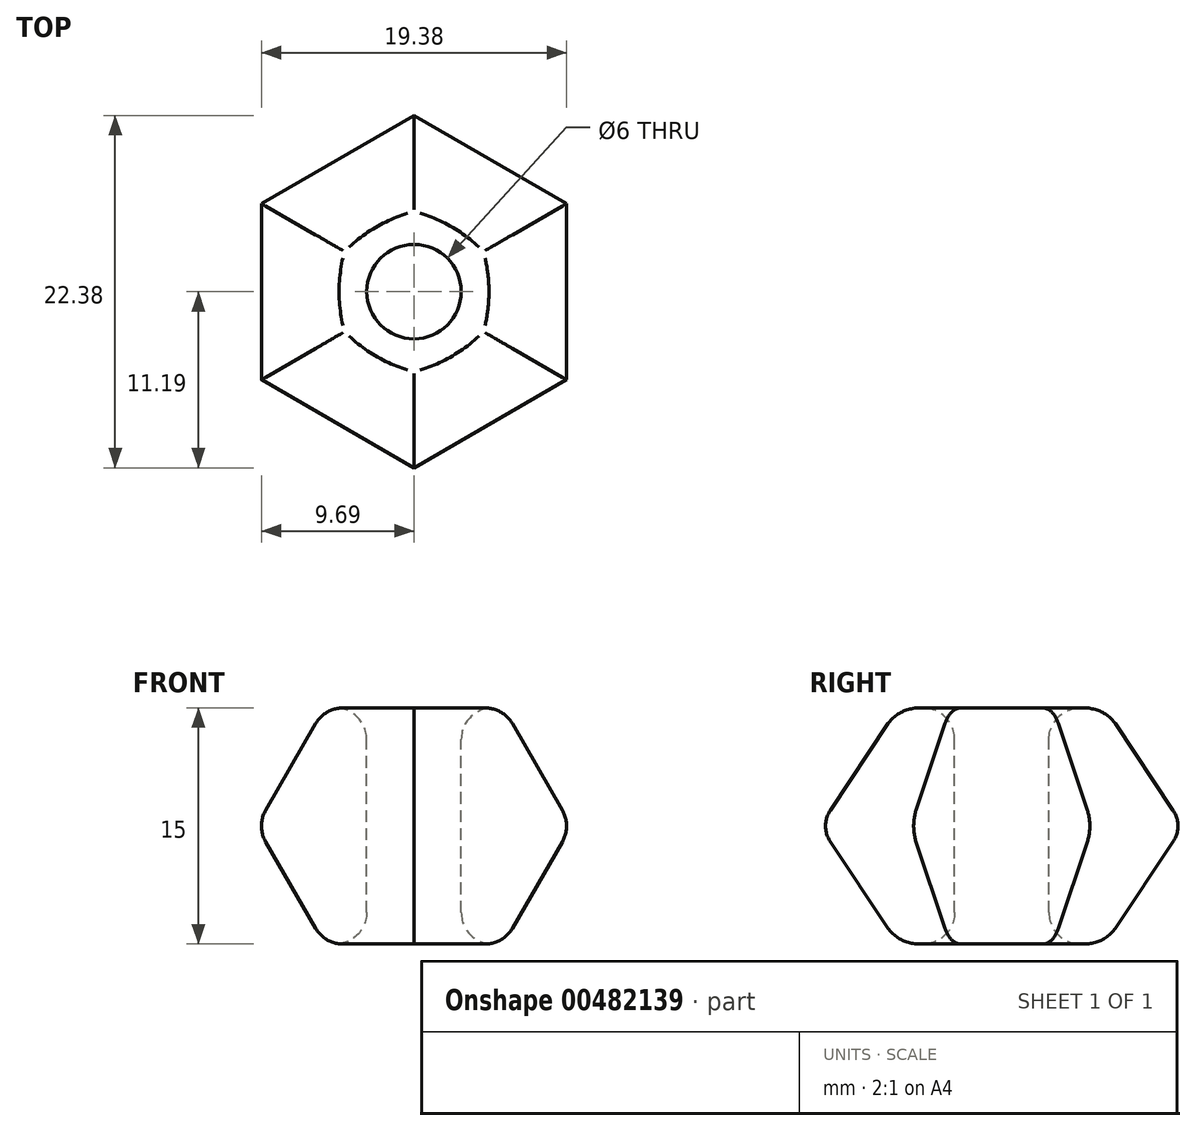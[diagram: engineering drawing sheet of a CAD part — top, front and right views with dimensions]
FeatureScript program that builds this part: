
annotation { "Feature Type Name" : "Feature", "Feature Type Description" : "" }
export const myFeature = defineFeature(function(context is Context, id is Id, definition is map)
    precondition{}
    {
        {
            var Q0;
            Q0=qCreatedBy(makeId("Top.planeOp"),FACE);
            var sketch = newSketch(context, id + "F0", { "sketchPlane" : qUnion([Q0])});
            skCircle(sketch, "E0.cCircle", {"center": v(0, 0) * mm, "radius": 10 * mm, "construction": true});
            skLineSegment(sketch, "E0.0", {"start": v(10, 5.77) * mm, "end": v(10, -5.77) * mm});
            skLineSegment(sketch, "E0.1", {"start": v(10, -5.77) * mm, "end": v(0, -11.55) * mm});
            skLineSegment(sketch, "E0.2", {"start": v(0, -11.55) * mm, "end": v(-10, -5.77) * mm});
            skLineSegment(sketch, "E0.3", {"start": v(-10, -5.77) * mm, "end": v(-10, 5.77) * mm});
            skLineSegment(sketch, "E0.4", {"start": v(-10, 5.77) * mm, "end": v(0, 11.55) * mm});
            skLineSegment(sketch, "E0.5", {"start": v(0, 11.55) * mm, "end": v(10, 5.77) * mm});
            skPoint(sketch, "E0.0.midPoint", {"position": v(10, 0) * mm});
            skSolve(sketch);
        }
        {
            var Q0;
            Q0 = qSketchRegion(id + "F0", true);
            extrude(context, id + "F1", {"entities" : qUnion([Q0]), "endBound" : BoundingType.SYMMETRIC, "depth" : 15 * mm, "hasDraft" : true, "draftAngle" : 30 * degree, "draftPullDirection" : true});
        }
        {
            var Q0;
            Q0=makeQuery(id+"F1.opExtrude","CAP_FACE",FACE,{"disambiguationData":[OSD([sQuery(id+"F0.wireOp",EDGE,"E0.0"),sQuery(id+"F0.wireOp",EDGE,"E0.1"),sQuery(id+"F0.wireOp",EDGE,"E0.2"),sQuery(id+"F0.wireOp",EDGE,"E0.3"),sQuery(id+"F0.wireOp",EDGE,"E0.4"),sQuery(id+"F0.wireOp",EDGE,"E0.5")])],"isStart":false});
            var sketch = newSketch(context, id + "F2", { "sketchPlane" : qUnion([Q0])});
            skCircle(sketch, "E1", {"center": v(0, 0) * mm, "radius": 3 * mm});
            skSolve(sketch);
        }
        {
            var Q0;
            Q0 = qSketchRegion(id + "F2", true);
            extrude(context, id + "F3", {"entities" : qUnion([Q0]), "operationType" : NewBodyOperationType.REMOVE, "endBound" : BoundingType.THROUGH_ALL, "oppositeDirection" : true, "depth" : 15 * mm});
        }
        {
            var Q0;
            {var subQ0=makeQuery(id+"F1.opExtrude","SWEPT_FACE",FACE,{"disambiguationData":[OSD([sQuery(id+"F0.wireOp",EDGE,"E0.5")])]});Q0=makeQuery(id+"F1.*.booleanUnion.opBoolean","MERGE",EDGE,{"derivedFrom":[makeQuery(id+"F1.*.split.splitOp","SPLIT_SURFACE_INTERSECT",EDGE,{"derivedFrom":[subQ0]}),makeQuery(id+"F1.*.split.splitOp","SPLIT_SURFACE_INTERSECT",EDGE,{"derivedFrom":[subQ0],"isFromBackBody":true})]});}
            var Q1;
            {var subQ0=makeQuery(id+"F1.opExtrude","SWEPT_FACE",FACE,{"disambiguationData":[OSD([sQuery(id+"F0.wireOp",EDGE,"E0.0")])]});Q1=makeQuery(id+"F1.*.booleanUnion.opBoolean","MERGE",EDGE,{"derivedFrom":[makeQuery(id+"F1.*.split.splitOp","SPLIT_SURFACE_INTERSECT",EDGE,{"derivedFrom":[subQ0]}),makeQuery(id+"F1.*.split.splitOp","SPLIT_SURFACE_INTERSECT",EDGE,{"derivedFrom":[subQ0],"isFromBackBody":true})]});}
            var Q2;
            {var subQ0=makeQuery(id+"F1.opExtrude","SWEPT_FACE",FACE,{"disambiguationData":[OSD([sQuery(id+"F0.wireOp",EDGE,"E0.1")])]});Q2=makeQuery(id+"F1.*.booleanUnion.opBoolean","MERGE",EDGE,{"derivedFrom":[makeQuery(id+"F1.*.split.splitOp","SPLIT_SURFACE_INTERSECT",EDGE,{"derivedFrom":[subQ0]}),makeQuery(id+"F1.*.split.splitOp","SPLIT_SURFACE_INTERSECT",EDGE,{"derivedFrom":[subQ0],"isFromBackBody":true})]});}
            var Q3;
            {var subQ0=makeQuery(id+"F1.opExtrude","SWEPT_FACE",FACE,{"disambiguationData":[OSD([sQuery(id+"F0.wireOp",EDGE,"E0.2")])]});Q3=makeQuery(id+"F1.*.booleanUnion.opBoolean","MERGE",EDGE,{"derivedFrom":[makeQuery(id+"F1.*.split.splitOp","SPLIT_SURFACE_INTERSECT",EDGE,{"derivedFrom":[subQ0]}),makeQuery(id+"F1.*.split.splitOp","SPLIT_SURFACE_INTERSECT",EDGE,{"derivedFrom":[subQ0],"isFromBackBody":true})]});}
            var Q4;
            {var subQ0=makeQuery(id+"F1.opExtrude","SWEPT_FACE",FACE,{"disambiguationData":[OSD([sQuery(id+"F0.wireOp",EDGE,"E0.3")])]});Q4=makeQuery(id+"F1.*.booleanUnion.opBoolean","MERGE",EDGE,{"derivedFrom":[makeQuery(id+"F1.*.split.splitOp","SPLIT_SURFACE_INTERSECT",EDGE,{"derivedFrom":[subQ0]}),makeQuery(id+"F1.*.split.splitOp","SPLIT_SURFACE_INTERSECT",EDGE,{"derivedFrom":[subQ0],"isFromBackBody":true})]});}
            var Q5;
            {var subQ0=makeQuery(id+"F1.opExtrude","SWEPT_FACE",FACE,{"disambiguationData":[OSD([sQuery(id+"F0.wireOp",EDGE,"E0.4")])]});Q5=makeQuery(id+"F1.*.booleanUnion.opBoolean","MERGE",EDGE,{"derivedFrom":[makeQuery(id+"F1.*.split.splitOp","SPLIT_SURFACE_INTERSECT",EDGE,{"derivedFrom":[subQ0]}),makeQuery(id+"F1.*.split.splitOp","SPLIT_SURFACE_INTERSECT",EDGE,{"derivedFrom":[subQ0],"isFromBackBody":true})]});}
            var Q6;
            Q6=makeQuery(id+"F1.opExtrude","CAP_EDGE",EDGE,{"disambiguationData":[OSD([sQuery(id+"F0.wireOp",EDGE,"E0.0")])],"isStart":true});
            var Q7;
            Q7=makeQuery(id+"F1.opExtrude","CAP_EDGE",EDGE,{"disambiguationData":[OSD([sQuery(id+"F0.wireOp",EDGE,"E0.5")])],"isStart":true});
            var Q8;
            Q8=makeQuery(id+"F1.opExtrude","CAP_EDGE",EDGE,{"disambiguationData":[OSD([sQuery(id+"F0.wireOp",EDGE,"E0.4")])],"isStart":true});
            var Q9;
            Q9=makeQuery(id+"F1.opExtrude","CAP_EDGE",EDGE,{"disambiguationData":[OSD([sQuery(id+"F0.wireOp",EDGE,"E0.3")])],"isStart":true});
            var Q10;
            Q10=makeQuery(id+"F1.opExtrude","CAP_EDGE",EDGE,{"disambiguationData":[OSD([sQuery(id+"F0.wireOp",EDGE,"E0.2")])],"isStart":true});
            var Q11;
            Q11=makeQuery(id+"F1.opExtrude","CAP_EDGE",EDGE,{"disambiguationData":[OSD([sQuery(id+"F0.wireOp",EDGE,"E0.1")])],"isStart":true});
            var Q12;
            Q12=makeQuery(id+"F1.opExtrude","CAP_EDGE",EDGE,{"disambiguationData":[OSD([sQuery(id+"F0.wireOp",EDGE,"E0.1")])],"isStart":false});
            var Q13;
            Q13=makeQuery(id+"F1.opExtrude","CAP_EDGE",EDGE,{"disambiguationData":[OSD([sQuery(id+"F0.wireOp",EDGE,"E0.2")])],"isStart":false});
            var Q14;
            Q14=makeQuery(id+"F1.opExtrude","CAP_EDGE",EDGE,{"disambiguationData":[OSD([sQuery(id+"F0.wireOp",EDGE,"E0.3")])],"isStart":false});
            var Q15;
            Q15=makeQuery(id+"F1.opExtrude","CAP_EDGE",EDGE,{"disambiguationData":[OSD([sQuery(id+"F0.wireOp",EDGE,"E0.4")])],"isStart":false});
            var Q16;
            Q16=makeQuery(id+"F1.opExtrude","CAP_EDGE",EDGE,{"disambiguationData":[OSD([sQuery(id+"F0.wireOp",EDGE,"E0.5")])],"isStart":false});
            var Q17;
            Q17=makeQuery(id+"F1.opExtrude","CAP_EDGE",EDGE,{"disambiguationData":[OSD([sQuery(id+"F0.wireOp",EDGE,"E0.0")])],"isStart":false});
            var Q18;
            Q18=makeQuery(id+"F3.boolean.opBoolean","INTERSECT",EDGE,{"derivedFrom":[makeQuery(id+"F1.opExtrude","CAP_FACE",FACE,{"disambiguationData":[OSD([sQuery(id+"F0.wireOp",EDGE,"E0.0"),sQuery(id+"F0.wireOp",EDGE,"E0.1"),sQuery(id+"F0.wireOp",EDGE,"E0.2"),sQuery(id+"F0.wireOp",EDGE,"E0.3"),sQuery(id+"F0.wireOp",EDGE,"E0.4"),sQuery(id+"F0.wireOp",EDGE,"E0.5")])],"isStart":true}),makeQuery(id+"F3.opExtrude","SWEPT_FACE",FACE,{"disambiguationData":[OSD([sQuery(id+"F2.wireOp",EDGE,"E1")])]})]});
            var Q19;
            Q19=makeQuery(id+"F3.boolean.opBoolean","COPY",FACE,{"derivedFrom":makeQuery(id+"F3.opExtrude","SWEPT_FACE",FACE,{"disambiguationData":[OSD([sQuery(id+"F2.wireOp",EDGE,"E1")])]})});
            fillet(context, id + "F4", {"entities" : qUnion([Q0, Q1, Q2, Q3, Q4, Q5, Q6, Q7, Q8, Q9, Q10, Q11, Q12, Q13, Q14, Q15, Q16, Q17, Q18, Q19]), "radius" : 2 * mm, "tangentPropagation" : true, "allowEdgeOverflow" : false});
        }
    });
